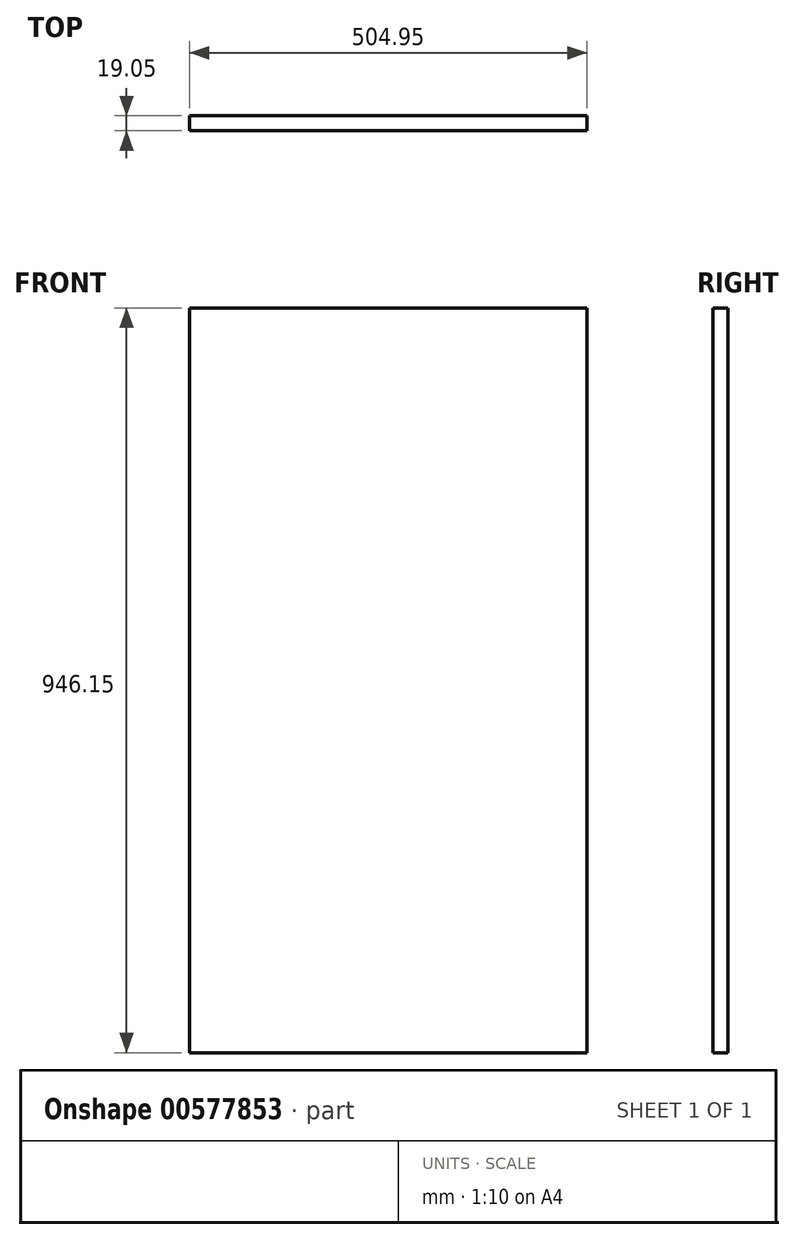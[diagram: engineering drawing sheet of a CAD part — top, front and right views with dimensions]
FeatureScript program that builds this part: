
annotation { "Feature Type Name" : "Feature", "Feature Type Description" : "" }
export const myFeature = defineFeature(function(context is Context, id is Id, definition is map)
    precondition{}
    {
        {
            var Q0;
            Q0=qCreatedBy(makeId("Front.planeOp"),FACE);
            var sketch = newSketch(context, id + "F0", { "sketchPlane" : qUnion([Q0])});
            skLineSegment(sketch, "E0.bottom", {"start": v(0, 0) * mm, "end": v(504.95, 0) * mm});
            skLineSegment(sketch, "E0.top", {"start": v(0, 946.15) * mm, "end": v(504.95, 946.15) * mm});
            skLineSegment(sketch, "E0.left", {"start": v(0, 0) * mm, "end": v(0, 946.15) * mm});
            skLineSegment(sketch, "E0.right", {"start": v(504.95, 0) * mm, "end": v(504.95, 946.15) * mm});
            skSolve(sketch);
        }
        {
            var Q0;
            Q0=makeQuery(id+"F0.imprint","IMPRINT",FACE,{"disambiguationData":[TD([[makeQuery(id+"F0.imprint","IMPRINT",EDGE,{"derivedFrom":sQuery(id+"F0.wireOp",EDGE,"E0.bottom")}),1.0]])]});
            extrude(context, id + "F1", {"entities" : qUnion([Q0]), "depth" : 19.05 * mm, "offsetDistance" : 25.4 * mm});
        }
    });
